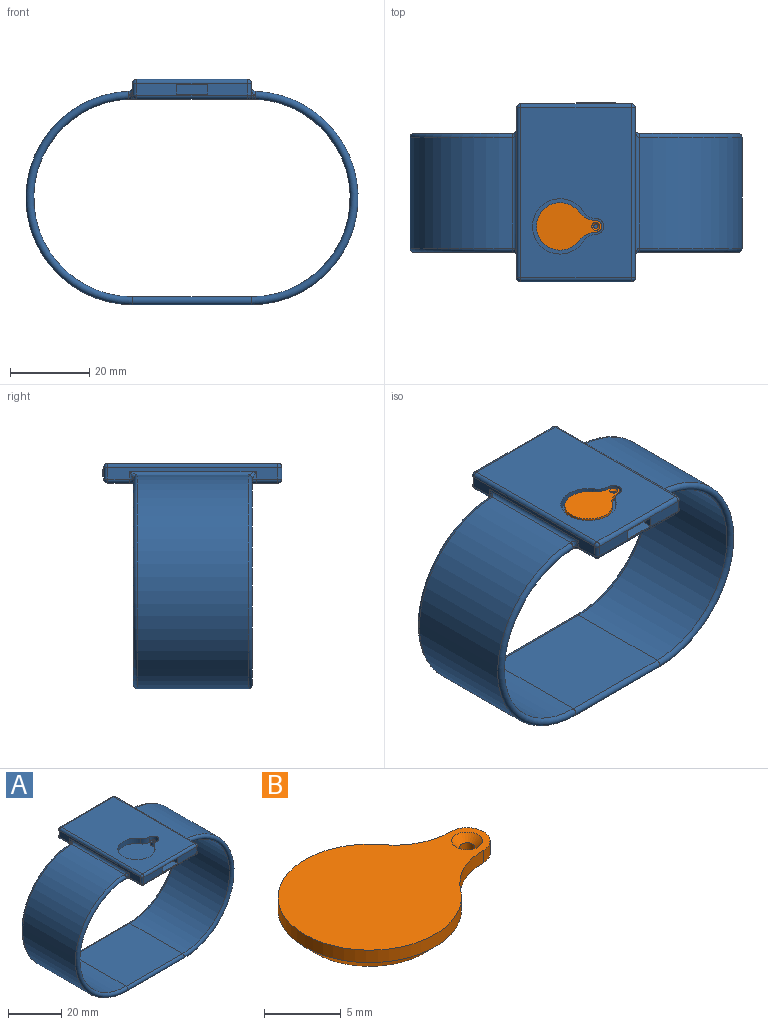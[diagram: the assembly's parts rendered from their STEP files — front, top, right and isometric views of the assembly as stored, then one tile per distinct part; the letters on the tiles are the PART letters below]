
ASSEMBLY  parts=2 mates=1
PART A: 87 faces, bbox 88.4x45.4x59.2 mm
  f0: cylinder r=1mm len=2mm, axis (0,0,1), area 9.4mm2, adj f83,f84
  f1: plane 43x28mm, normal (0,0,1), area 1033.8mm2, adj f23,f24,f27,f28,f79,f80,f81,f82
  f2: plane 28x3mm, normal (0,-1,0), area 64mm2, adj f19,f20,f22,f23,f63,f64,f65,f66
  f3: plane 43x3mm, normal (-1,0,0), area 65.6mm2, adj f13,f14,f15,f19,f24,f29,f48,f61
  f4: plane 43x3mm, normal (1,0,0), area 65.6mm2, adj f16,f17,f18,f22,f27,f32,f53,f56
  f5: plane 28x3mm, normal (0,1,0), area 64.2mm2, adj f28,f29,f31,f32,f68,f69,f70,f71
  f6: plane 43x30mm, normal (0,0,-1), area 1263.1mm2, adj f10,f12,f20,f31,f48,f49,f52,f53
  f7: cylinder r=27mm len=53.98mm, axis (0,1,0), area 2348mm2, adj f8,f15,f37,f38,f44,f45
  f8: plane 30x28mm, normal (0,0,-1), area 840mm2, adj f7,f9,f36,f43
  f9: cylinder r=27mm len=53.98mm, axis (0,1,0), area 2348mm2, adj f8,f18,f34,f35,f41,f42
  f10: cylinder r=25mm len=50mm, axis (0,1,0), area 2199.3mm2, adj f6,f11,f35,f42,f51,f58
  f11: plane 30x28mm, normal (0,0,1), area 840mm2, adj f10,f12,f36,f43
  f12: cylinder r=25mm len=50mm, axis (0,1,0), area 2199.3mm2, adj f6,f11,f37,f44,f50,f59
  f13: cylinder r=1mm len=2mm, axis (0,0,-1), area 1.1mm2, adj f3,f39,f49,f50
  f14: cylinder r=1mm len=2mm, axis (0,0,1), area 1.1mm2, adj f3,f46,f59,f60
  f15: cylinder r=1mm len=32mm, axis (0,1,0), area 45.3mm2, adj f3,f7,f39,f46
  f16: cylinder r=1mm len=2mm, axis (0,0,-1), area 1.1mm2, adj f4,f33,f51,f52
  f17: cylinder r=1mm len=2mm, axis (0,0,1), area 1.1mm2, adj f4,f40,f57,f58
  f18: cylinder r=1mm len=32mm, axis (0,1,0), area 45.3mm2, adj f4,f9,f33,f40
  f19: cylinder r=1mm len=3mm, axis (0,0,1), area 4.7mm2, adj f2,f3,f21,f47
  f20: cylinder r=1mm len=28mm, axis (1,0,0), area 44mm2, adj f2,f6,f47,f54
  f21: sphere r=1mm, area 1.6mm2, adj f19,f23,f24
  f22: cylinder r=1mm len=3mm, axis (0,0,-1), area 4.7mm2, adj f2,f4,f25,f54
  f23: cylinder r=1mm len=28mm, axis (-1,0,0), area 44mm2, adj f1,f2,f21,f25
  f24: cylinder r=1mm len=43mm, axis (0,1,0), area 67.5mm2, adj f1,f3,f21,f26
  f25: sphere r=1mm, area 1.6mm2, adj f22,f23,f27
  f26: sphere r=1mm, area 1.6mm2, adj f24,f28,f29
  f27: cylinder r=1mm len=43mm, axis (0,-1,0), area 67.5mm2, adj f1,f4,f25,f30
  f28: cylinder r=1mm len=28mm, axis (1,0,0), area 44mm2, adj f1,f5,f26,f30
  f29: cylinder r=1mm len=3mm, axis (0,0,-1), area 4.7mm2, adj f3,f5,f26,f62
  f30: sphere r=1mm, area 1.6mm2, adj f27,f28,f32
  f31: cylinder r=1mm len=28mm, axis (-1,0,0), area 44mm2, adj f5,f6,f55,f62
  f32: cylinder r=1mm len=3mm, axis (0,0,1), area 4.7mm2, adj f4,f5,f30,f55
  f33: bspline ~2x2mm, area 1.8mm2, adj f16,f18,f34
  f34: bspline ~1.01x1.01mm, area 0.1mm2, adj f9,f33,f35,f51
  f35: torus R=26mm, axis (0,-1,0), area 253.5mm2, adj f9,f10,f34,f36,f51
  f36: cylinder r=1mm len=30mm, axis (-1,0,0), area 94.2mm2, adj f8,f11,f35,f37
  f37: torus R=26mm, axis (0,-1,0), area 253.5mm2, adj f7,f12,f36,f38,f50
  f38: bspline ~1.01x1.01mm, area 0.1mm2, adj f7,f37,f39,f50
  f39: bspline ~2x2mm, area 1.8mm2, adj f13,f15,f38
  f40: bspline ~2x2mm, area 1.8mm2, adj f17,f18,f41
  f41: bspline ~1.01x1.01mm, area 0.1mm2, adj f9,f40,f42,f58
  f42: torus R=26mm, axis (0,-1,0), area 253.5mm2, adj f9,f10,f41,f43,f58
  f43: cylinder r=1mm len=30mm, axis (1,0,0), area 94.2mm2, adj f8,f11,f42,f44
  f44: torus R=26mm, axis (0,-1,0), area 253.5mm2, adj f7,f12,f43,f45,f59
  f45: bspline ~1.01x1.01mm, area 0.1mm2, adj f7,f44,f46,f59
  f46: bspline ~2x2mm, area 1.8mm2, adj f14,f15,f45
  f47: sphere r=1mm, area 1.6mm2, adj f19,f20,f48
  f48: cylinder r=1mm len=5.5mm, axis (0,-1,0), area 8.6mm2, adj f3,f6,f47,f49
  f49: torus R=2mm, axis (0,0,1), area 2.2mm2, adj f6,f13,f48,f50
  f50: bspline ~1.48x1.22mm, area 1.1mm2, adj f12,f13,f37,f38,f49
  f51: bspline ~1.48x1.22mm, area 1.1mm2, adj f10,f16,f34,f35,f52
  f52: torus R=2mm, axis (0,0,1), area 2.2mm2, adj f6,f16,f51,f53
  f53: cylinder r=1mm len=5.5mm, axis (0,1,0), area 8.6mm2, adj f4,f6,f52,f54
  f54: sphere r=1mm, area 1.6mm2, adj f20,f22,f53
  f55: sphere r=1mm, area 1.6mm2, adj f31,f32,f56
  f56: cylinder r=1mm len=5.5mm, axis (0,1,0), area 8.6mm2, adj f4,f6,f55,f57
  f57: torus R=2mm, axis (0,0,1), area 2.2mm2, adj f6,f17,f56,f58
  f58: bspline ~1.48x1.22mm, area 1.1mm2, adj f10,f17,f41,f42,f57
  f59: bspline ~1.48x1.22mm, area 1.1mm2, adj f12,f14,f44,f45,f60
  f60: torus R=2mm, axis (0,0,1), area 2.2mm2, adj f6,f14,f59,f61
  f61: cylinder r=1mm len=5.5mm, axis (0,-1,0), area 8.6mm2, adj f3,f6,f60,f62
  f62: sphere r=1mm, area 1.6mm2, adj f29,f31,f61
  f63: plane 4x2.5mm, normal (-1,0,0), area 10mm2, adj f2,f64,f66,f67
  f64: plane 8x4mm, normal (0,0,-1), area 32mm2, adj f2,f63,f65,f67
  f65: plane 4x2.5mm, normal (1,0,0), area 10mm2, adj f2,f64,f66,f67
  f66: plane 8x4mm, normal (0,0,1), area 32mm2, adj f2,f63,f65,f67
  f67: plane 8x2.5mm, normal (0,-1,0), area 20mm2, adj f63,f64,f65,f66
  f68: cylinder r=0.9mm len=1.8mm, axis (0,-1,0), area 0.8mm2, adj f5,f69,f71,f73
  f69: plane 8.2x0.3mm, normal (0,0,1), area 2.5mm2, adj f5,f68,f70,f74
  f70: cylinder r=0.9mm len=1.8mm, axis (0,-1,0), area 0.8mm2, adj f5,f69,f71,f76
  f71: plane 8.2x0.3mm, normal (0,0,-1), area 2.5mm2, adj f5,f68,f70,f75
  f72: plane 9.8x1.6mm, normal (0,1,0), area 15.1mm2, adj f73,f74,f75,f76
  f73: torus R=0.8mm, axis (0,1,0), area 0.4mm2, adj f68,f72,f74,f75
  f74: cylinder r=0.1mm len=8.2mm, axis (-1,0,0), area 1.3mm2, adj f69,f72,f73,f76
  f75: cylinder r=0.1mm len=8.2mm, axis (1,0,0), area 1.3mm2, adj f71,f72,f73,f76
  f76: torus R=0.8mm, axis (0,1,0), area 0.4mm2, adj f70,f72,f74,f75
  f77: cylinder r=0.9mm len=1.8mm, axis (0,1,0), area 2.3mm2, adj f5,f78
  f78: plane 1.8x1.8mm, normal (0,1,0), area 2.5mm2, adj f77
  f79: cylinder r=3.6mm len=3.06mm, axis (0,0,1), area 9.1mm2, adj f1,f80,f82,f83
  f80: cylinder r=7mm len=14mm, axis (0,0,1), area 90.5mm2, adj f1,f79,f81,f83
  f81: cylinder r=3.6mm len=3.06mm, axis (0,0,1), area 9.1mm2, adj f1,f80,f82,f83
  f82: cylinder r=2mm len=4mm, axis (0,0,1), area 15.7mm2, adj f1,f79,f81,f83
  f83: plane 18x14mm, normal (0,0,1), area 167.1mm2, adj f0,f79,f80,f81,f82
  f84: plane 2x2mm, normal (0,0,1), area 2.4mm2, adj f0,f86
  f85: plane 1x1mm, normal (0,0,1), area 0.8mm2, adj f86
  f86: cylinder r=0.5mm len=1.5mm, axis (0,0,1), area 4.7mm2, adj f84,f85
PART B: 12 faces, bbox 16.5x12x2 mm
  f0: cylinder r=1.5mm len=3mm, axis (0,0,1), area 4.7mm2, adj f1,f3,f5,f11
  f1: cylinder r=5.25mm len=4.2mm, axis (0,0,1), area 4.9mm2, adj f0,f2,f5,f9
  f2: cylinder r=6mm len=12mm, axis (0,0,1), area 30mm2, adj f1,f3,f5,f8
  f3: cylinder r=5.25mm len=4.2mm, axis (0,0,1), area 4.9mm2, adj f0,f2,f5,f10
  f4: plane 14x10mm, normal (0,0,-1), area 86.6mm2, adj f6,f8,f9,f10
  f5: plane 16.5x12mm, normal (0,0,1), area 125.5mm2, adj f0,f1,f2,f3,f7
  f6: cylinder r=0.5mm len=1.5mm, axis (0,0,1), area 4.7mm2, adj f4,f7,f11
  f7: cone r=0.5mm half-angle=45deg, axis (0,0,1), area 3.3mm2, adj f5,f6
  f8: cone r=6mm half-angle=45deg, axis (0,0,1), area 38.9mm2, adj f2,f4,f9,f10
  f9: cone r=5.25mm half-angle=45deg, axis (0,0,-1), area 7.5mm2, adj f1,f4,f8,f11
  f10: cone r=6.25mm half-angle=45deg, axis (0,0,-1), area 7.5mm2, adj f3,f4,f8,f11
  f11: cone r=0.5mm half-angle=45deg, axis (0,0,1), area 4.4mm2, adj f0,f6,f9,f10
PLACE A at identity
PLACE B t=(-4,-8.5,4.75)mm
MATE slider A.f0 <-> B.f6  axis (0,0,1) through (5,-8.5,4)mm
